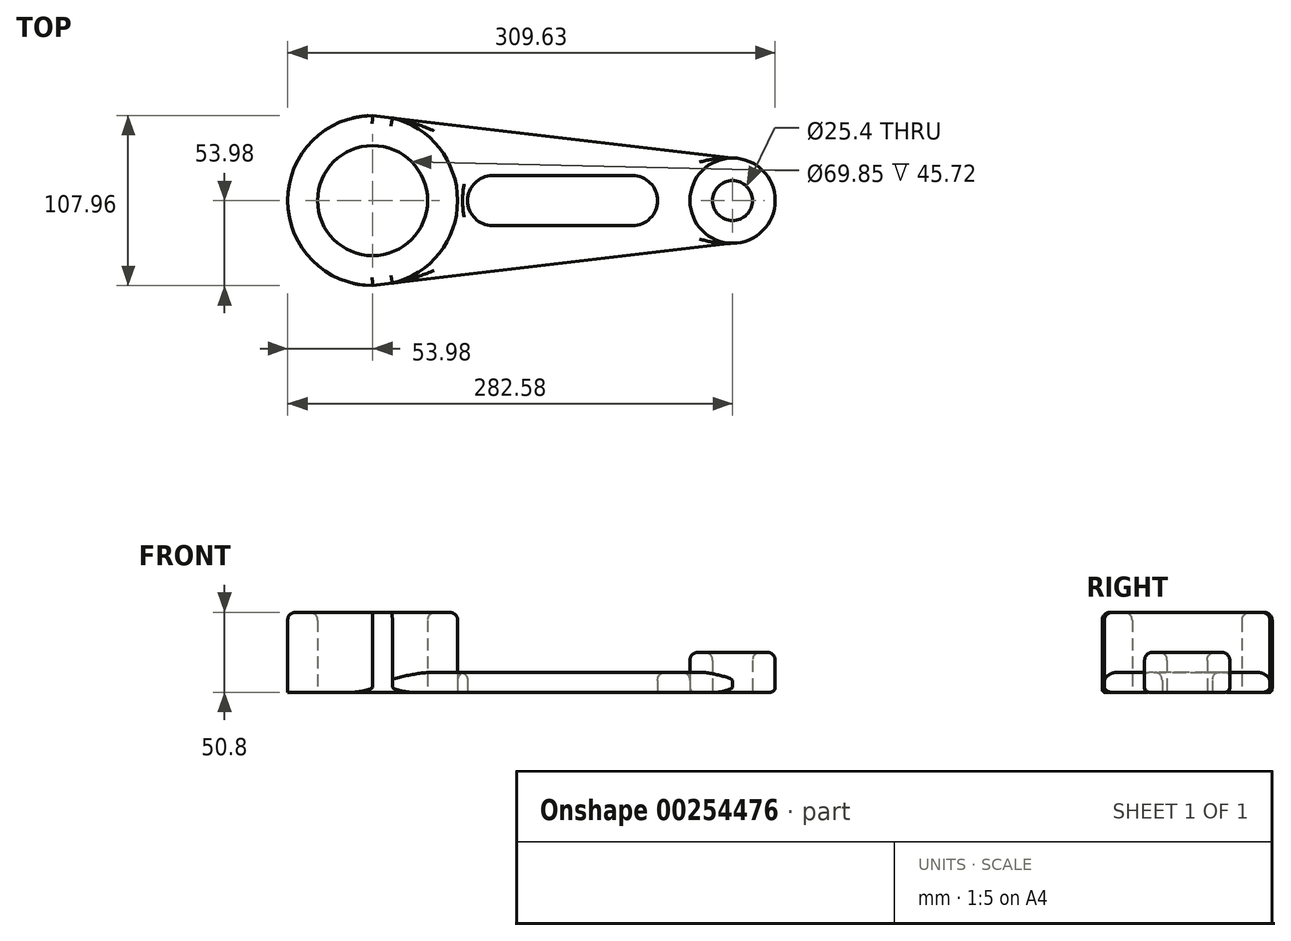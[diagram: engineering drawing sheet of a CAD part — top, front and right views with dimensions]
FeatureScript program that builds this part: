
annotation { "Feature Type Name" : "Feature", "Feature Type Description" : "" }
export const myFeature = defineFeature(function(context is Context, id is Id, definition is map)
    precondition{}
    {
        {
            var Q0;
            Q0=qCreatedBy(makeId("Top.planeOp"),FACE);
            var sketch = newSketch(context, id + "F0", { "sketchPlane" : qUnion([Q0])});
            skCircle(sketch, "E0", {"center": v(0, 0) * mm, "radius": 34.93 * mm});
            skCircle(sketch, "E1", {"center": v(0, 0) * mm, "radius": 53.98 * mm});
            skLineSegment(sketch, "E2", {"start": v(0, -107.01) * mm, "end": v(228.6, -107.01) * mm});
            skCircle(sketch, "E3", {"center": v(228.6, 0) * mm, "radius": 12.7 * mm});
            skCircle(sketch, "E4", {"center": v(228.6, 0) * mm, "radius": 27.05 * mm});
            skLineSegment(sketch, "E5", {"start": v(0, -65.2) * mm, "end": v(76.2, -65.2) * mm});
            skLineSegment(sketch, "E6", {"start": v(76.2, -65.2) * mm, "end": v(165.1, -65.2) * mm});
            skArc(sketch, "E7", {"start": v(76.2, 15.88) * mm, "mid": v(60.33, 0) * mm, "end": v(76.2, -15.88) * mm});
            skArc(sketch, "E8", {"start": v(165.1, -15.88) * mm, "mid": v(180.98, 0) * mm, "end": v(165.1, 15.88) * mm});
            skLineSegment(sketch, "E9", {"start": v(76.2, -15.88) * mm, "end": v(165.1, -15.88) * mm});
            skLineSegment(sketch, "E10", {"start": v(76.2, 15.87) * mm, "end": v(165.1, 15.87) * mm});
            skLineSegment(sketch, "E11", {"start": v(0, 53.97) * mm, "end": v(228.6, 27.05) * mm});
            skLineSegment(sketch, "E12", {"start": v(0, -53.97) * mm, "end": v(228.6, -27.05) * mm});
            skSolve(sketch);
        }
        {
            var Q0;
            Q0=makeQuery(id+"F0.imprint","IMPRINT",FACE,{"disambiguationData":[TD([[makeQuery(id+"F0.imprint","IMPRINT",EDGE,{"derivedFrom":sQuery(id+"F0.wireOp",EDGE,"E0")}),-1.0]])]});
            extrude(context, id + "F1", {"entities" : qUnion([Q0]), "depth" : 50.8 * mm});
        }
        {
            var Q0;
            Q0=makeQuery(id+"F0.imprint","IMPRINT",FACE,{"disambiguationData":[TD([[makeQuery(id+"F0.imprint","IMPRINT",EDGE,{"derivedFrom":sQuery(id+"F0.wireOp",EDGE,"E3")}),-1.0]])]});
            extrude(context, id + "F2", {"entities" : qUnion([Q0]), "depth" : 25.4 * mm});
        }
        {
            var Q0;
            Q0=makeQuery(id+"F0.imprint","IMPRINT",FACE,{"disambiguationData":[TD([[makeQuery(id+"F0.imprint","IMPRINT",EDGE,{"derivedFrom":sQuery(id+"F0.wireOp",EDGE,"E7")}),-1.0]])]});
            extrude(context, id + "F3", {"entities" : qUnion([Q0]), "depth" : 12.7 * mm});
        }
        {
            var Q0;
            Q0=makeQuery(id+"F3.opExtrude","CAP_EDGE",EDGE,{"disambiguationData":[OSD([sQuery(id+"F0.wireOp",EDGE,"E12")])],"isStart":true});
            var Q1;
            Q1=makeQuery(id+"F1.opExtrude","CAP_EDGE",EDGE,{"disambiguationData":[OSD([sQuery(id+"F0.wireOp",EDGE,"E12")])],"isStart":true});
            var Q2;
            {var subQ0=sQuery(id+"F0.wireOp",EDGE,"E1");Q2=makeQuery(id+"F1.opExtrude","CAP_EDGE",EDGE,{"disambiguationData":[OSD([subQ0]),TDD([makeQuery(id+"F0.imprint","IMPRINT",EDGE,{"disambiguationData":[TD([[makeQuery(id+"F0.imprint","INTERSECT",VERTEX,{"disambiguationData":[OD(0.0)],"derivedFrom":[subQ0,sQuery(id+"F0.wireOp",EDGE,"E11")]}),-1.0]])],"derivedFrom":subQ0})])],"isStart":true});}
            var Q3;
            Q3=makeQuery(id+"F2.opExtrude","CAP_EDGE",EDGE,{"disambiguationData":[OSD([sQuery(id+"F0.wireOp",EDGE,"E4")])],"isStart":true});
            var Q4;
            Q4=makeQuery(id+"F1.opExtrude","CAP_EDGE",EDGE,{"disambiguationData":[OSD([sQuery(id+"F0.wireOp",EDGE,"E11")])],"isStart":true});
            var Q5;
            Q5=makeQuery(id+"F3.opExtrude","CAP_EDGE",EDGE,{"disambiguationData":[OSD([sQuery(id+"F0.wireOp",EDGE,"E11")])],"isStart":true});
            fillet(context, id + "F4", {"entities" : qUnion([Q0, Q1, Q2, Q3, Q4, Q5]), "radius" : 3.17 * mm, "tangentPropagation" : true, "allowEdgeOverflow" : false});
        }
        {
            var Q0;
            Q0=makeQuery(id+"F3.opExtrude","CAP_EDGE",EDGE,{"disambiguationData":[OSD([sQuery(id+"F0.wireOp",EDGE,"E12")])],"isStart":false});
            var Q1;
            Q1=makeQuery(id+"F1.opExtrude","CAP_FACE",FACE,{"disambiguationData":[OSD([sQuery(id+"F0.wireOp",EDGE,"E0"),sQuery(id+"F0.wireOp",EDGE,"E1"),sQuery(id+"F0.wireOp",EDGE,"E11"),sQuery(id+"F0.wireOp",EDGE,"E12")])],"isStart":false});
            var Q2;
            Q2=makeQuery(id+"F3.opExtrude","CAP_FACE",FACE,{"disambiguationData":[OSD([sQuery(id+"F0.wireOp",EDGE,"E1"),sQuery(id+"F0.wireOp",EDGE,"E4"),sQuery(id+"F0.wireOp",EDGE,"E7"),sQuery(id+"F0.wireOp",EDGE,"E8"),sQuery(id+"F0.wireOp",EDGE,"E9"),sQuery(id+"F0.wireOp",EDGE,"E10"),sQuery(id+"F0.wireOp",EDGE,"E11"),sQuery(id+"F0.wireOp",EDGE,"E12")])],"isStart":false});
            var Q3;
            Q3=makeQuery(id+"F2.opExtrude","CAP_FACE",FACE,{"disambiguationData":[OSD([sQuery(id+"F0.wireOp",EDGE,"E3"),sQuery(id+"F0.wireOp",EDGE,"E4")])],"isStart":false});
            fillet(context, id + "F5", {"entities" : qUnion([Q0, Q1, Q2, Q3]), "radius" : 5.08 * mm, "tangentPropagation" : true, "allowEdgeOverflow" : false});
        }
    });
